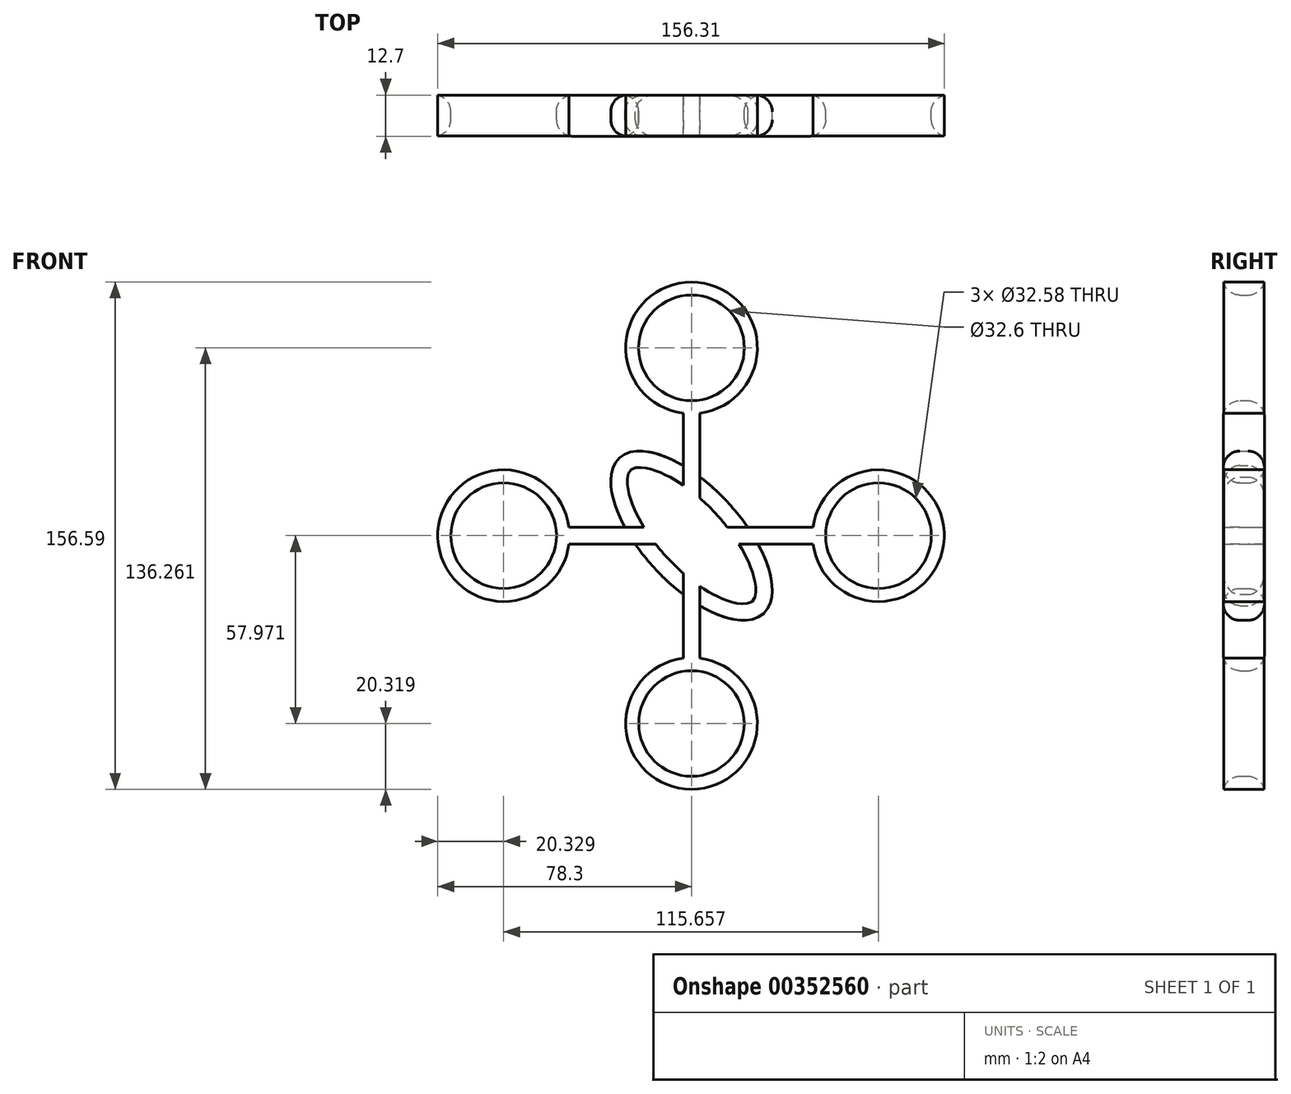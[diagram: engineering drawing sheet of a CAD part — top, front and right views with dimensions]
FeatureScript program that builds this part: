
annotation { "Feature Type Name" : "Feature", "Feature Type Description" : "" }
export const myFeature = defineFeature(function(context is Context, id is Id, definition is map)
    precondition{}
    {
        {
            var Q0;
            Q0=qCreatedBy(makeId("Front.planeOp"),FACE);
            var sketch = newSketch(context, id + "F0", { "sketchPlane" : qUnion([Q0])});
            skPoint(sketch, "E0.middle", {"position": v(0, 0) * mm});
            skLineSegment(sketch, "E1.left", {"start": v(2.57, 37.81) * mm, "end": v(2.57, 18.13) * mm});
            skLineSegment(sketch, "E1.right", {"start": v(-2.57, 37.81) * mm, "end": v(-2.57, 21.6) * mm});
            skLineSegment(sketch, "E2.top", {"start": v(37.52, 2.57) * mm, "end": v(17.37, 2.57) * mm});
            skEllipse(sketch, "E3", {"center": v(0, 0) * mm, "majorRadius": 32.74 * mm, "minorRadius": 15.2 * mm, "majorAxis": v(-0.68, 0.73)});
            skPoint(sketch, "E4.centerSnap0", {"position": v(-60.54, 0) * mm});
            skArc(sketch, "E5", {"start": v(37.52, -2.57) * mm, "mid": v(78.01, 0) * mm, "end": v(37.52, 2.57) * mm});
            skPoint(sketch, "E5.centerSnap0", {"position": v(60.54, 0) * mm});
            skCircle(sketch, "E6", {"center": v(0, 57.97) * mm, "radius": 20.32 * mm});
            skPoint(sketch, "E6.centerSnap0", {"position": v(0, 60.54) * mm});
            skCircle(sketch, "E7", {"center": v(-57.97, 0) * mm, "radius": 20.33 * mm});
            skCircle(sketch, "E8", {"center": v(0, -57.97) * mm, "radius": 20.31 * mm});
            skPoint(sketch, "E8.centerSnap0", {"position": v(0, -60.54) * mm});
            skPoint(sketch, "E9.orphan", {"position": v(-12.85, 12.85) * mm});
            skLineSegment(sketch, "E10.trimOffspring", {"start": v(-20.53, 2.57) * mm, "end": v(-37.8, 2.57) * mm});
            skLineSegment(sketch, "E11.trimOffspring", {"start": v(-17.37, -2.57) * mm, "end": v(-37.8, -2.57) * mm});
            skPoint(sketch, "E12.orphan", {"position": v(12.85, 12.85) * mm});
            skPoint(sketch, "E13.orphan", {"position": v(12.85, -12.85) * mm});
            skLineSegment(sketch, "E14.trimOffspring", {"start": v(2.57, -21.6) * mm, "end": v(2.57, -37.82) * mm});
            skLineSegment(sketch, "E15.trimOffspring", {"start": v(-2.57, -18.13) * mm, "end": v(-2.57, -37.82) * mm});
            skPoint(sketch, "E0.top.start.orphan", {"position": v(-12.85, -12.85) * mm});
            skCircle(sketch, "E16", {"center": v(0, 57.97) * mm, "radius": 16.3 * mm});
            skCircle(sketch, "E17", {"center": v(57.69, 0) * mm, "radius": 16.29 * mm});
            skCircle(sketch, "E18", {"center": v(-57.97, 0) * mm, "radius": 16.3 * mm});
            skCircle(sketch, "E19", {"center": v(0, -57.97) * mm, "radius": 16.3 * mm});
            skPoint(sketch, "E20.orphan", {"position": v(-60.54, 2.57) * mm});
            skPoint(sketch, "E2.right.start.orphan", {"position": v(-60.54, -2.57) * mm});
            skPoint(sketch, "E21.orphan", {"position": v(-2.57, 60.54) * mm});
            skPoint(sketch, "E22.orphan", {"position": v(2.57, 60.54) * mm});
            skLineSegment(sketch, "E23.trimOffspring", {"start": v(37.52, -2.57) * mm, "end": v(20.53, -2.57) * mm});
            skPoint(sketch, "E24.orphan", {"position": v(60.54, 2.57) * mm});
            skPoint(sketch, "E2.left.start.orphan", {"position": v(60.54, -2.57) * mm});
            skPoint(sketch, "E25.orphan", {"position": v(2.57, -60.54) * mm});
            skPoint(sketch, "E1.top.end.orphan", {"position": v(-2.57, -60.54) * mm});
            skLineSegment(sketch, "E26.left", {"start": v(37.52, 2.57) * mm, "end": v(37.52, -2.57) * mm});
            skSolve(sketch);
        }
        {
            var Q0;
            Q0 = qSketchRegion(id + "F0", true);
            extrude(context, id + "F1", {"entities" : qUnion([Q0]), "endBound" : BoundingType.SYMMETRIC, "depth" : 12.7 * mm});
        }
        {
            var Q0;
            Q0=makeQuery(id+"F1.opExtrude","CAP_EDGE",EDGE,{"disambiguationData":[OSD([sQuery(id+"F0.wireOp",EDGE,"E16")])],"isStart":false});
            var Q1;
            Q1=makeQuery(id+"F1.opExtrude","CAP_EDGE",EDGE,{"disambiguationData":[OSD([sQuery(id+"F0.wireOp",EDGE,"E18")])],"isStart":false});
            var Q2;
            Q2=makeQuery(id+"F1.opExtrude","CAP_EDGE",EDGE,{"disambiguationData":[OSD([sQuery(id+"F0.wireOp",EDGE,"E17")])],"isStart":false});
            var Q3;
            Q3=makeQuery(id+"F1.opExtrude","CAP_EDGE",EDGE,{"disambiguationData":[OSD([sQuery(id+"F0.wireOp",EDGE,"E19")])],"isStart":false});
            var Q4;
            {var subQ0=sQuery(id+"F0.wireOp",EDGE,"E3");Q4=makeQuery(id+"F1.opExtrude","CAP_EDGE",EDGE,{"disambiguationData":[OSD([subQ0]),TDD([makeQuery(id+"F0.imprint","IMPRINT",EDGE,{"disambiguationData":[TD([[makeQuery(id+"F0.imprint","INTERSECT",VERTEX,{"derivedFrom":[subQ0,sQuery(id+"F0.wireOp",EDGE,"E11.trimOffspring")]}),-1.0]])],"derivedFrom":subQ0})])],"isStart":false});}
            var Q5;
            {var subQ0=sQuery(id+"F0.wireOp",EDGE,"E3");Q5=makeQuery(id+"F1.opExtrude","CAP_EDGE",EDGE,{"disambiguationData":[OSD([subQ0]),TDD([makeQuery(id+"F0.imprint","IMPRINT",EDGE,{"disambiguationData":[TD([[makeQuery(id+"F0.imprint","INTERSECT",VERTEX,{"derivedFrom":[sQuery(id+"F0.wireOp",EDGE,"E1.right"),subQ0]}),-1.0]])],"derivedFrom":subQ0})])],"isStart":false});}
            var Q6;
            {var subQ0=sQuery(id+"F0.wireOp",EDGE,"E3");Q6=makeQuery(id+"F1.opExtrude","CAP_EDGE",EDGE,{"disambiguationData":[OSD([subQ0]),TDD([makeQuery(id+"F0.imprint","IMPRINT",EDGE,{"disambiguationData":[TD([[makeQuery(id+"F0.imprint","INTERSECT",VERTEX,{"derivedFrom":[sQuery(id+"F0.wireOp",EDGE,"E1.left"),subQ0]}),1.0]])],"derivedFrom":subQ0})])],"isStart":false});}
            var Q7;
            {var subQ0=sQuery(id+"F0.wireOp",EDGE,"E3");Q7=makeQuery(id+"F1.opExtrude","CAP_EDGE",EDGE,{"disambiguationData":[OSD([subQ0]),TDD([makeQuery(id+"F0.imprint","IMPRINT",EDGE,{"disambiguationData":[TD([[makeQuery(id+"F0.imprint","INTERSECT",VERTEX,{"derivedFrom":[subQ0,sQuery(id+"F0.wireOp",EDGE,"E14.trimOffspring")]}),-1.0]])],"derivedFrom":subQ0})])],"isStart":false});}
            fillet(context, id + "F2", {"entities" : qUnion([Q0, Q1, Q2, Q3, Q4, Q5, Q6, Q7]), "radius" : 5.08 * mm, "tangentPropagation" : true, "allowEdgeOverflow" : false});
        }
        {
            var Q0;
            Q0=makeQuery(id+"F1.opExtrude","CAP_EDGE",EDGE,{"disambiguationData":[OSD([sQuery(id+"F0.wireOp",EDGE,"E18")])],"isStart":true});
            var Q1;
            Q1=makeQuery(id+"F1.opExtrude","CAP_EDGE",EDGE,{"disambiguationData":[OSD([sQuery(id+"F0.wireOp",EDGE,"E19")])],"isStart":true});
            var Q2;
            Q2=makeQuery(id+"F1.opExtrude","CAP_EDGE",EDGE,{"disambiguationData":[OSD([sQuery(id+"F0.wireOp",EDGE,"E16")])],"isStart":true});
            var Q3;
            Q3=makeQuery(id+"F1.opExtrude","CAP_EDGE",EDGE,{"disambiguationData":[OSD([sQuery(id+"F0.wireOp",EDGE,"E17")])],"isStart":true});
            fillet(context, id + "F3", {"entities" : qUnion([Q0, Q1, Q2, Q3]), "radius" : 5.08 * mm, "tangentPropagation" : true, "allowEdgeOverflow" : false});
        }
        {
            var Q0;
            {var subQ0=sQuery(id+"F0.wireOp",EDGE,"E3");Q0=makeQuery(id+"F1.opExtrude","CAP_EDGE",EDGE,{"disambiguationData":[OSD([subQ0]),TDD([makeQuery(id+"F0.imprint","IMPRINT",EDGE,{"disambiguationData":[TD([[makeQuery(id+"F0.imprint","INTERSECT",VERTEX,{"derivedFrom":[sQuery(id+"F0.wireOp",EDGE,"E1.left"),subQ0]}),1.0]])],"derivedFrom":subQ0})])],"isStart":true});}
            var Q1;
            {var subQ0=sQuery(id+"F0.wireOp",EDGE,"E3");Q1=makeQuery(id+"F1.opExtrude","CAP_EDGE",EDGE,{"disambiguationData":[OSD([subQ0]),TDD([makeQuery(id+"F0.imprint","IMPRINT",EDGE,{"disambiguationData":[TD([[makeQuery(id+"F0.imprint","INTERSECT",VERTEX,{"derivedFrom":[sQuery(id+"F0.wireOp",EDGE,"E1.right"),subQ0]}),-1.0]])],"derivedFrom":subQ0})])],"isStart":true});}
            var Q2;
            {var subQ0=sQuery(id+"F0.wireOp",EDGE,"E3");Q2=makeQuery(id+"F1.opExtrude","CAP_EDGE",EDGE,{"disambiguationData":[OSD([subQ0]),TDD([makeQuery(id+"F0.imprint","IMPRINT",EDGE,{"disambiguationData":[TD([[makeQuery(id+"F0.imprint","INTERSECT",VERTEX,{"derivedFrom":[subQ0,sQuery(id+"F0.wireOp",EDGE,"E11.trimOffspring")]}),-1.0]])],"derivedFrom":subQ0})])],"isStart":true});}
            var Q3;
            {var subQ0=sQuery(id+"F0.wireOp",EDGE,"E3");Q3=makeQuery(id+"F1.opExtrude","CAP_EDGE",EDGE,{"disambiguationData":[OSD([subQ0]),TDD([makeQuery(id+"F0.imprint","IMPRINT",EDGE,{"disambiguationData":[TD([[makeQuery(id+"F0.imprint","INTERSECT",VERTEX,{"derivedFrom":[subQ0,sQuery(id+"F0.wireOp",EDGE,"E14.trimOffspring")]}),-1.0]])],"derivedFrom":subQ0})])],"isStart":true});}
            fillet(context, id + "F4", {"entities" : qUnion([Q0, Q1, Q2, Q3]), "radius" : 5.08 * mm, "tangentPropagation" : true, "allowEdgeOverflow" : false});
        }
    });
